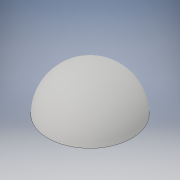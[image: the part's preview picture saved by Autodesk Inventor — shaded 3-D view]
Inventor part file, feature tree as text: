
AUTODESK INVENTOR PART (.ipt)
format: ipt  version: 2018 (Build 220112000, 112)  size: 110,080 bytes
history: native  units: in
note: dims shown in document units (in); Inventor stores cm internally (conversion verified against a paired STEP export)
features: revolve x1, sketch x1
ambient origin geometry x8: Origin, YZ Plane, XZ Plane, XY Plane, X Axis, Y Axis, Z Axis, Center Point
bodies: Solid1 (feature_tree)
feature tree (2):
  revolve  "Revolution1"  Angle=180.0deg
  sketch  "Sketch1"  dims[d0=0.5in d1=180.0deg]
